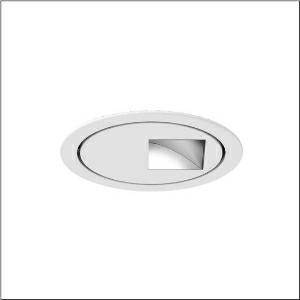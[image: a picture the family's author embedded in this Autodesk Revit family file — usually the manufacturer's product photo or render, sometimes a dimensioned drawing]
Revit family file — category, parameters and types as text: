
# Revit family: lunis_11_mini_round_51dk11b72wf21
name_source: partatom
category: Lighting Fixtures
units: mm (PartAtom-declared; Revit-internal decimal feet)

## family parameters
Cut with Voids When Loaded = No
Host = Face
Light Source = No
Part Type = Normal
Room Calculation Point = No
Round Connector Dimension = Use Diameter
Shared = No

## types (1)
- Lunis 11 mini round (1 x LED 3000K / CRI = 80 (unbekannt), 2380 lm, 3000K)
    Apparent Load = 28 VA
    CIE Flux Codes = 44 77 97 100 100
    Color Rendering = 80
    Color Temperature = 3000K
    Default Elevation = 1800 mm
    Description = Lunis 11 mini round, downlight, light control with wallwasher, of highly reflective aluminium, highly specular, light emission: direct distribution, LED rated luminous flux: 2.380lm, light colour: 830, control gear: ECG, with terminal, 3-pole, mains connection: 220..230V, AC/DC, 0/50..60Hz, LED module, luminaire module, of aluminium, highly specular, white, diameter: 176mm, clamping range: 1..40mm, recessing ring, of plastic, traffic white (RAL 9016), protection rating (complete): IP20, insulation class (complete): insulation class II (safety insulation), certification: CE, permissible ambient temperature for indoor applications: 0..+35°C, packaging unit: 1 piece
    Height = 0 mm  [stored 0 ft]
    Lamp = 1 x LED 3000K / CRI >= 80 (unbekannt)
    Lamp Light Flux = 2380 lm
    Lamp count = 1
    Length = 176 mm
    Luminous efficacy = 85 lm/W
    Manufacturer = Siteco
    ModVariant = No
    Model = 51DK11B72WF21
    Mounting Place = Ceiling
    Mounting Type = Recessed
    Number of Poles = 1
    OnlyDefault = Yes
    Power Factor = 1
    Product Name = Lunis 11 mini round
    Product group = downlight
    ProductGroupID = 401
    Protection Class = Protection class II
    Protection Degree = IP 20
    RLX_Detail_Level = 1
    RLX_Emergency_Light_Flux = 0 lm
    RLX_Emergency_Type = 0
    RLX_Emergency_Type_DB = No
    RlxData = <blob elided: 59277 chars, md5=5ae67938>
    Socket = socket
    Standby Power = 0 W
    System Light Flux = 2380 lm
    System Power = 28 W
    Type Comments = Product without accessories
    Type Image = l_1004772.jpg
    URL = http://relux.com
    VarID = ---
    Voltage = 0 V
    Weight = 0.00 kg
    Width = 176 mm

note: [stored X ft] marks values corroborated as IEEE doubles in the binary element streams (Revit-internal decimal feet)

## geometry (parser evidence)
native form markers: Blend x4, Sweep x12
no freeform markers — native parametric forms only
